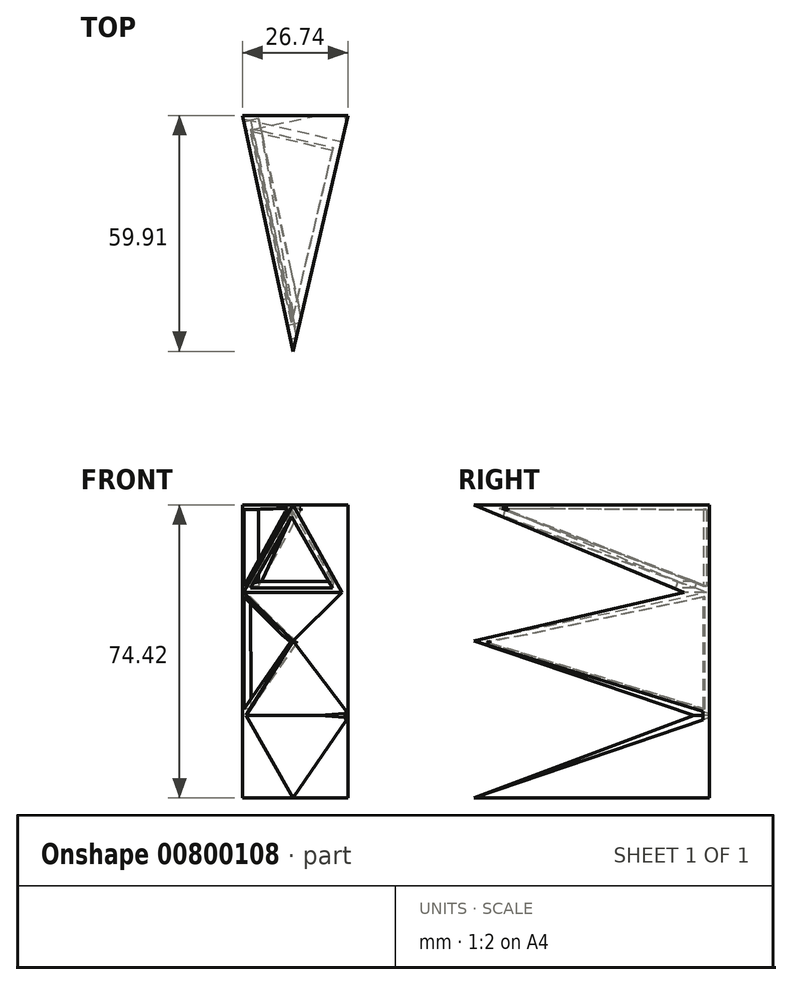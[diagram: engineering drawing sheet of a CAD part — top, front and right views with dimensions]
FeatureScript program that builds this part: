
annotation { "Feature Type Name" : "Feature", "Feature Type Description" : "" }
export const myFeature = defineFeature(function(context is Context, id is Id, definition is map)
    precondition{}
    {
        {
            var Q0;
            Q0=qCreatedBy(makeId("Top.planeOp"),FACE);
            var sketch = newSketch(context, id + "F0", { "sketchPlane" : qUnion([Q0])});
            skLineSegment(sketch, "E0", {"start": v(-12.8, 24.93) * mm, "end": v(13.94, 24.93) * mm});
            skLineSegment(sketch, "E1", {"start": v(13.94, 24.93) * mm, "end": v(0, -34.98) * mm});
            skLineSegment(sketch, "E2", {"start": v(0, -34.98) * mm, "end": v(-12.8, 24.93) * mm});
            skSolve(sketch);
        }
        {
            var Q0;
            Q0 = qSketchRegion(id + "F0", true);
            extrude(context, id + "F1", {"entities" : qUnion([Q0]), "depth" : 74.42 * mm, "offsetDistance" : 25.4 * mm});
        }
        {
            var Q0;
            Q0=makeQuery(id+"F1.opExtrude","SWEPT_FACE",FACE,{"disambiguationData":[OSD([sQuery(id+"F0.wireOp",EDGE,"E1")])]});
            var sketch = newSketch(context, id + "F2", { "sketchPlane" : qUnion([Q0])});
            skLineSegment(sketch, "E3", {"start": v(-34.07, 74.42) * mm, "end": v(20.7, 52.22) * mm});
            skLineSegment(sketch, "E4", {"start": v(20.7, 52.22) * mm, "end": v(-34.07, 39.8) * mm});
            skLineSegment(sketch, "E5", {"start": v(-34.07, 39.8) * mm, "end": v(-34.07, 74.42) * mm});
            skSolve(sketch);
        }
        {
            var Q0;
            Q0 = qSketchRegion(id + "F2", true);
            extrude(context, id + "F3", {"entities" : qUnion([Q0]), "operationType" : NewBodyOperationType.REMOVE, "oppositeDirection" : true, "depth" : 25.4 * mm, "offsetDistance" : 25.4 * mm});
        }
        {
            var Q0;
            Q0=makeQuery(id+"F1.opExtrude","SWEPT_FACE",FACE,{"disambiguationData":[OSD([sQuery(id+"F0.wireOp",EDGE,"E2")])]});
            var sketch = newSketch(context, id + "F4", { "sketchPlane" : qUnion([Q0])});
            skLineSegment(sketch, "E6", {"start": v(34.2, 39.8) * mm, "end": v(-23, 20.97) * mm});
            skLineSegment(sketch, "E7", {"start": v(-23, 20.97) * mm, "end": v(34.2, 0) * mm});
            skLineSegment(sketch, "E8", {"start": v(34.2, 0) * mm, "end": v(34.2, 39.8) * mm});
            skSolve(sketch);
        }
        {
            var Q0;
            Q0 = qSketchRegion(id + "F4", true);
            extrude(context, id + "F5", {"entities" : qUnion([Q0]), "operationType" : NewBodyOperationType.REMOVE, "oppositeDirection" : true, "depth" : 25.4 * mm, "offsetDistance" : 25.4 * mm});
        }
        {
            var Q0;
            Q0=makeQuery(id+"F1.opExtrude","SWEPT_FACE",FACE,{"disambiguationData":[OSD([sQuery(id+"F0.wireOp",EDGE,"E2")])]});
            var sketch = newSketch(context, id + "F6", { "sketchPlane" : qUnion([Q0])});
            skLineSegment(sketch, "E9", {"start": v(-25.47, 73.24) * mm, "end": v(-25.47, 53.76) * mm});
            skLineSegment(sketch, "E10", {"start": v(-25.47, 53.76) * mm, "end": v(22.02, 71.48) * mm});
            skLineSegment(sketch, "E11", {"start": v(22.02, 71.48) * mm, "end": v(25.38, 72.73) * mm});
            skLineSegment(sketch, "E12", {"start": v(25.38, 72.73) * mm, "end": v(27.55, 73.53) * mm});
            skLineSegment(sketch, "E13", {"start": v(27.55, 73.53) * mm, "end": v(14.33, 73.53) * mm});
            skLineSegment(sketch, "E14", {"start": v(14.33, 73.53) * mm, "end": v(-25.47, 73.24) * mm});
            skSolve(sketch);
        }
        {
            var Q0;
            Q0 = qSketchRegion(id + "F6", true);
            extrude(context, id + "F7", {"entities" : qUnion([Q0]), "operationType" : NewBodyOperationType.REMOVE, "oppositeDirection" : true, "depth" : 3.8 * mm, "offsetDistance" : 25.4 * mm});
        }
        {
            var Q0;
            Q0=makeQuery(id+"F1.opExtrude","SWEPT_FACE",FACE,{"disambiguationData":[OSD([sQuery(id+"F0.wireOp",EDGE,"E2")])]});
            var sketch = newSketch(context, id + "F8", { "sketchPlane" : qUnion([Q0])});
            skLineSegment(sketch, "E15", {"start": v(-25.45, 50.98) * mm, "end": v(20.8, 41.43) * mm});
            skLineSegment(sketch, "E16", {"start": v(20.8, 41.43) * mm, "end": v(31.07, 39.58) * mm});
            skLineSegment(sketch, "E17", {"start": v(31.07, 39.58) * mm, "end": v(16.84, 35.32) * mm});
            skLineSegment(sketch, "E18", {"start": v(16.84, 35.32) * mm, "end": v(-24.52, 22.92) * mm});
            skLineSegment(sketch, "E19", {"start": v(-24.52, 22.92) * mm, "end": v(-25.43, 22.64) * mm});
            skLineSegment(sketch, "E20", {"start": v(-25.43, 22.64) * mm, "end": v(-25.45, 50.98) * mm});
            skSolve(sketch);
        }
        {
            var Q0;
            Q0 = qSketchRegion(id + "F8", true);
            extrude(context, id + "F9", {"entities" : qUnion([Q0]), "operationType" : NewBodyOperationType.REMOVE, "oppositeDirection" : true, "depth" : 1.78 * mm, "offsetDistance" : 25.4 * mm});
        }
        {
            var Q0;
            Q0=makeQuery(id+"F3.boolean.opBoolean","COPY",FACE,{"derivedFrom":makeQuery(id+"F3.opExtrude","SWEPT_FACE",FACE,{"disambiguationData":[OSD([sQuery(id+"F2.wireOp",EDGE,"E3")])]})});
            var sketch = newSketch(context, id + "F10", { "sketchPlane" : qUnion([Q0])});
            skLineSegment(sketch, "E21", {"start": v(-5.2, 51.96) * mm, "end": v(-15.63, 0) * mm});
            skLineSegment(sketch, "E22", {"start": v(-15.63, 0) * mm, "end": v(5.22, 4.5) * mm});
            skLineSegment(sketch, "E23", {"start": v(5.22, 4.5) * mm, "end": v(-5.2, 51.96) * mm});
            skSolve(sketch);
        }
        {
            var Q0;
            Q0 = qSketchRegion(id + "F10", true);
            extrude(context, id + "F11", {"entities" : qUnion([Q0]), "operationType" : NewBodyOperationType.REMOVE, "oppositeDirection" : true, "depth" : 1.78 * mm, "offsetDistance" : 25.4 * mm});
        }
    });
